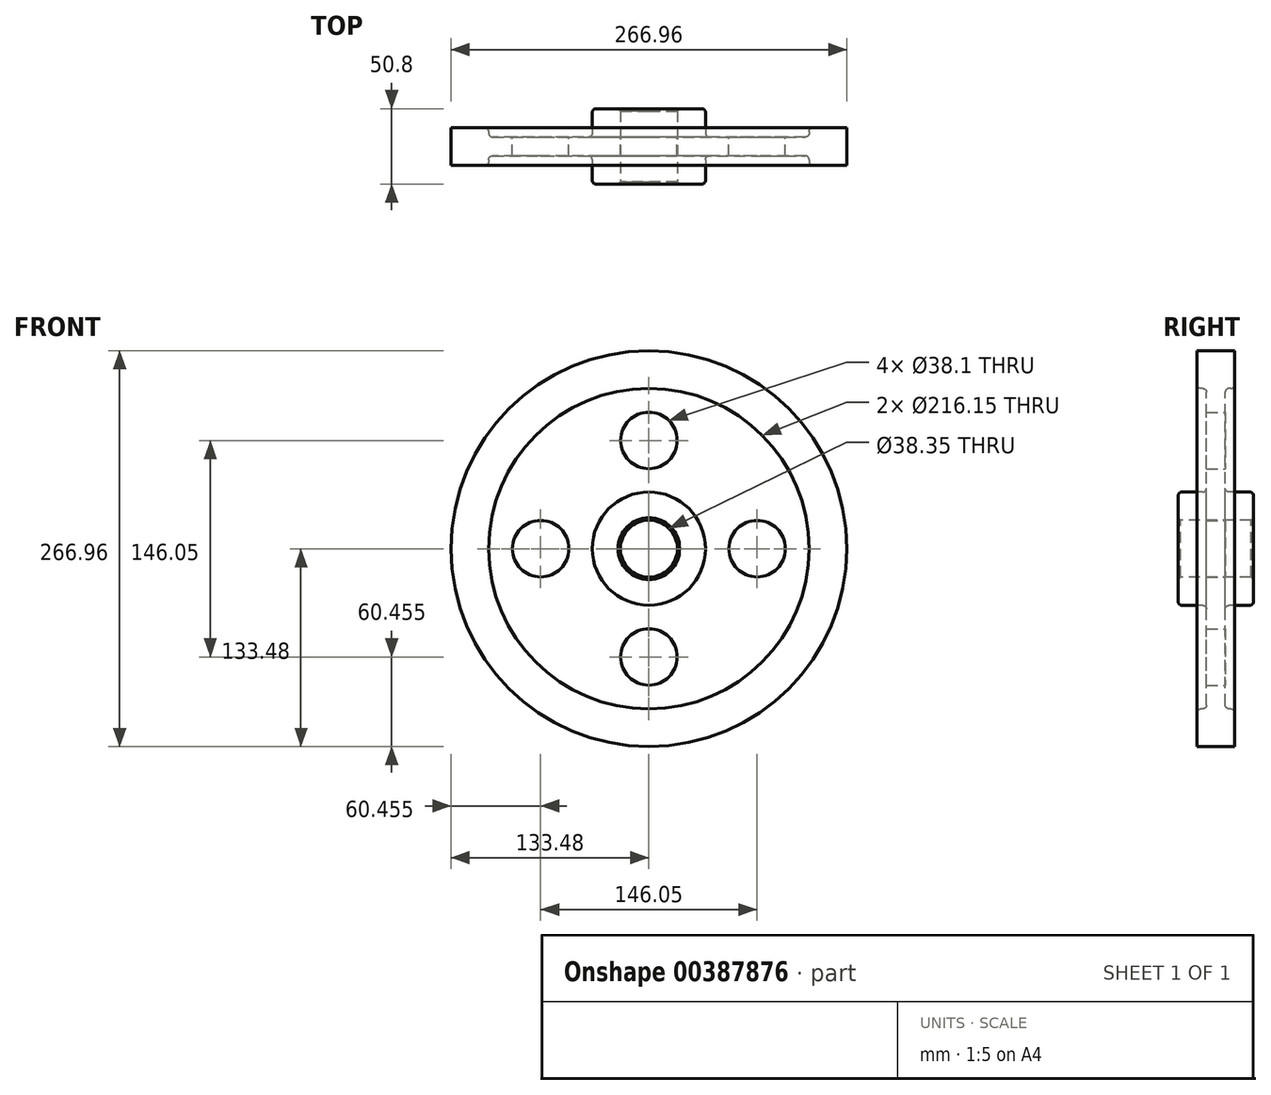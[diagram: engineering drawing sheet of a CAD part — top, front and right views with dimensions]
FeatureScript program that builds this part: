
annotation { "Feature Type Name" : "Feature", "Feature Type Description" : "" }
export const myFeature = defineFeature(function(context is Context, id is Id, definition is map)
    precondition{}
    {
        {
            var Q0;
            Q0=qCreatedBy(makeId("Right.planeOp"),FACE);
            var sketch = newSketch(context, id + "F0", { "sketchPlane" : qUnion([Q0])});
            skLineSegment(sketch, "E0", {"start": v(0, 0) * mm, "end": v(76.05, 0) * mm});
            skLineSegment(sketch, "E1", {"start": v(0, 0) * mm, "end": v(0, 28.7) * mm});
            skLineSegment(sketch, "E2", {"start": v(0, 28.7) * mm, "end": v(0, 73.15) * mm});
            skLineSegment(sketch, "E3", {"start": v(0, 73.15) * mm, "end": v(0, 108.08) * mm});
            skLineSegment(sketch, "E4.bottom", {"start": v(25.4, 19.18) * mm, "end": v(-25.4, 19.18) * mm});
            skLineSegment(sketch, "E4.top", {"start": v(25.4, 38.23) * mm, "end": v(6.35, 38.23) * mm});
            skLineSegment(sketch, "E4.left", {"start": v(25.4, 19.18) * mm, "end": v(25.4, 38.23) * mm});
            skLineSegment(sketch, "E4.right", {"start": v(-25.4, 19.18) * mm, "end": v(-25.4, 38.23) * mm});
            skPoint(sketch, "E4.middle", {"position": v(0, 28.7) * mm});
            skLineSegment(sketch, "E5.bottom", {"start": v(12.7, 108.08) * mm, "end": v(6.35, 108.08) * mm});
            skLineSegment(sketch, "E5.top", {"start": v(12.7, 133.48) * mm, "end": v(-12.7, 133.48) * mm});
            skLineSegment(sketch, "E5.left", {"start": v(12.7, 108.08) * mm, "end": v(12.7, 133.48) * mm});
            skLineSegment(sketch, "E5.right", {"start": v(-12.7, 108.08) * mm, "end": v(-12.7, 133.48) * mm});
            skPoint(sketch, "E5.middle", {"position": v(0, 120.78) * mm});
            skLineSegment(sketch, "E6.left", {"start": v(6.35, 32.84) * mm, "end": v(6.35, 113.46) * mm});
            skLineSegment(sketch, "E6.right", {"start": v(-6.35, 32.84) * mm, "end": v(-6.35, 113.46) * mm});
            skPoint(sketch, "E6.middle", {"position": v(0, 73.15) * mm});
            skLineSegment(sketch, "E7.trimOffspring", {"start": v(0, 113.46) * mm, "end": v(0, 120.78) * mm});
            skLineSegment(sketch, "E8.trimOffspring", {"start": v(-6.35, 108.08) * mm, "end": v(-12.7, 108.08) * mm});
            skLineSegment(sketch, "E9.trimOffspring", {"start": v(-6.35, 38.23) * mm, "end": v(-25.4, 38.23) * mm});
            skSolve(sketch);
        }
        {
            var Q0;
            {var subQ4=sQuery(id+"F0.wireOp",EDGE,"E4.top");Q0=makeQuery(id+"F0.imprint","IMPRINT",FACE,{"disambiguationData":[TD([[makeQuery(id+"F0.imprint","IMPRINT",EDGE,{"derivedFrom":subQ4}),1.0]])]});}
            var Q1;
            Q1=sQuery(id+"F0.wireOp",EDGE,"E0");
            revolve(context, id + "F1", {"entities" : qUnion([Q0]), "axis" : qUnion([Q1]), "revolveType" : RevolveType.FULL});
        }
        {
            var Q0;
            Q0=makeQuery(id+"F1.opRevolve","SWEPT_EDGE",EDGE,{"disambiguationData":[OSD([sQuery(id+"F0.wireOp",EDGE,"E4.top"),sQuery(id+"F0.wireOp",EDGE,"E6.left")])]});
            var Q1;
            Q1=makeQuery(id+"F1.opRevolve","SWEPT_EDGE",EDGE,{"disambiguationData":[OSD([sQuery(id+"F0.wireOp",EDGE,"E4.top"),sQuery(id+"F0.wireOp",EDGE,"E4.left")])]});
            var Q2;
            Q2=makeQuery(id+"F1.opRevolve","SWEPT_EDGE",EDGE,{"disambiguationData":[OSD([sQuery(id+"F0.wireOp",EDGE,"E5.bottom"),sQuery(id+"F0.wireOp",EDGE,"E6.left")])]});
            var Q3;
            Q3=makeQuery(id+"F1.opRevolve","SWEPT_EDGE",EDGE,{"disambiguationData":[OSD([sQuery(id+"F0.wireOp",EDGE,"E5.bottom"),sQuery(id+"F0.wireOp",EDGE,"E5.left")])]});
            var Q4;
            Q4=makeQuery(id+"F1.opRevolve","SWEPT_EDGE",EDGE,{"disambiguationData":[OSD([sQuery(id+"F0.wireOp",EDGE,"E6.right"),sQuery(id+"F0.wireOp",EDGE,"E9.trimOffspring")])]});
            var Q5;
            Q5=makeQuery(id+"F1.opRevolve","SWEPT_EDGE",EDGE,{"disambiguationData":[OSD([sQuery(id+"F0.wireOp",EDGE,"E4.right"),sQuery(id+"F0.wireOp",EDGE,"E9.trimOffspring")])]});
            var Q6;
            Q6=makeQuery(id+"F1.opRevolve","SWEPT_EDGE",EDGE,{"disambiguationData":[OSD([sQuery(id+"F0.wireOp",EDGE,"E6.right"),sQuery(id+"F0.wireOp",EDGE,"E8.trimOffspring")])]});
            var Q7;
            Q7=makeQuery(id+"F1.opRevolve","SWEPT_EDGE",EDGE,{"disambiguationData":[OSD([sQuery(id+"F0.wireOp",EDGE,"E5.right"),sQuery(id+"F0.wireOp",EDGE,"E8.trimOffspring")])]});
            fillet(context, id + "F2", {"entities" : qUnion([Q0, Q1, Q2, Q3, Q4, Q5, Q6, Q7]), "radius" : 2.54 * mm, "tangentPropagation" : true, "allowEdgeOverflow" : false});
        }
        {
            var Q0;
            Q0=makeQuery(id+"F1.opRevolve","SWEPT_EDGE",EDGE,{"disambiguationData":[OSD([sQuery(id+"F0.wireOp",EDGE,"E4.bottom"),sQuery(id+"F0.wireOp",EDGE,"E4.right")])]});
            var Q1;
            Q1=makeQuery(id+"F1.opRevolve","SWEPT_EDGE",EDGE,{"disambiguationData":[OSD([sQuery(id+"F0.wireOp",EDGE,"E4.bottom"),sQuery(id+"F0.wireOp",EDGE,"E4.left")])]});
            chamfer(context, id + "F3", {"entities" : qUnion([Q0, Q1]), "width" : 1.59 * mm, "tangentPropagation" : true});
        }
        {
            var Q0;
            Q0=makeQuery(id+"F1.opRevolve","SWEPT_FACE",FACE,{"disambiguationData":[OSD([sQuery(id+"F0.wireOp",EDGE,"E6.left")])]});
            var sketch = newSketch(context, id + "F4", { "sketchPlane" : qUnion([Q0])});
            skLineSegment(sketch, "E10", {"start": v(0, 0) * mm, "end": v(73.02, 0) * mm});
            skCircle(sketch, "E11", {"center": v(73.02, 0) * mm, "radius": 19.05 * mm});
            skCircle(sketch, "E12.1.0", {"center": v(0, 73.02) * mm, "radius": 19.05 * mm});
            skCircle(sketch, "E12.2.0", {"center": v(-73.02, 0) * mm, "radius": 19.05 * mm});
            skCircle(sketch, "E12.3.0", {"center": v(0, -73.02) * mm, "radius": 19.05 * mm});
            skPoint(sketch, "E12.center", {"position": v(0, 0) * mm});
            skSolve(sketch);
        }
        {
            var Q0;
            Q0=makeQuery(id+"F4.imprint","IMPRINT",FACE,{"disambiguationData":[TD([[makeQuery(id+"F4.imprint","IMPRINT",EDGE,{"derivedFrom":sQuery(id+"F4.wireOp",EDGE,"E11")}),1.0]])]});
            var Q1;
            Q1=makeQuery(id+"F4.imprint","IMPRINT",FACE,{"disambiguationData":[TD([[makeQuery(id+"F4.imprint","IMPRINT",EDGE,{"derivedFrom":sQuery(id+"F4.wireOp",EDGE,"E12.3.0")}),1.0]])]});
            var Q2;
            Q2=makeQuery(id+"F4.imprint","IMPRINT",FACE,{"disambiguationData":[TD([[makeQuery(id+"F4.imprint","IMPRINT",EDGE,{"derivedFrom":sQuery(id+"F4.wireOp",EDGE,"E12.1.0")}),1.0]])]});
            var Q3;
            Q3=makeQuery(id+"F4.imprint","IMPRINT",FACE,{"disambiguationData":[TD([[makeQuery(id+"F4.imprint","IMPRINT",EDGE,{"derivedFrom":sQuery(id+"F4.wireOp",EDGE,"E12.2.0")}),1.0]])]});
            extrude(context, id + "F5", {"entities" : qUnion([Q0, Q1, Q2, Q3]), "operationType" : NewBodyOperationType.REMOVE, "oppositeDirection" : true, "depth" : 25.4 * mm});
        }
    });
